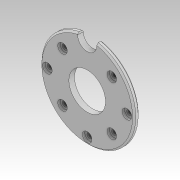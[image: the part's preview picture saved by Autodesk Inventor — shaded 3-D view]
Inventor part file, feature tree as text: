
AUTODESK INVENTOR PART (.ipt)
format: ipt  version: 2020 (Build 240168000, 168)  size: 176,640 bytes
history: native  units: mm
features: extrude x3, sketch x3, chamfer x1
ambient origin geometry x8: Origin, YZ Plane, XZ Plane, XY Plane, X Axis, Y Axis, Z Axis, Center Point
bodies: Solid1 (feature_tree)
feature tree (7):
  extrude  "Extrusion1"  Depth=3.3mm
  extrude  "Extrusion2"  Depth=31.0mm
  extrude  "Extrusion3"  Depth=3.3mm
  chamfer  "Chamfer1"  Distance=3.5mm
  sketch  "Sketch1"  dims[d0=59.0mm d1=3.3mm]
  sketch  "Sketch2"  dims[d2=23.0mm d3=31.0mm]
  sketch  "Sketch3"  dims[d4=50.0mm d5=3.3mm d6=3.5mm d7=0.0mm d8=6.0mm d9=1.5mm d10=0.0mm d11=1.0mm d12=2.0mm d13=45.0deg d14=2.0mm d15=6.0mm d16=0.0mm d17=0.0mm]
